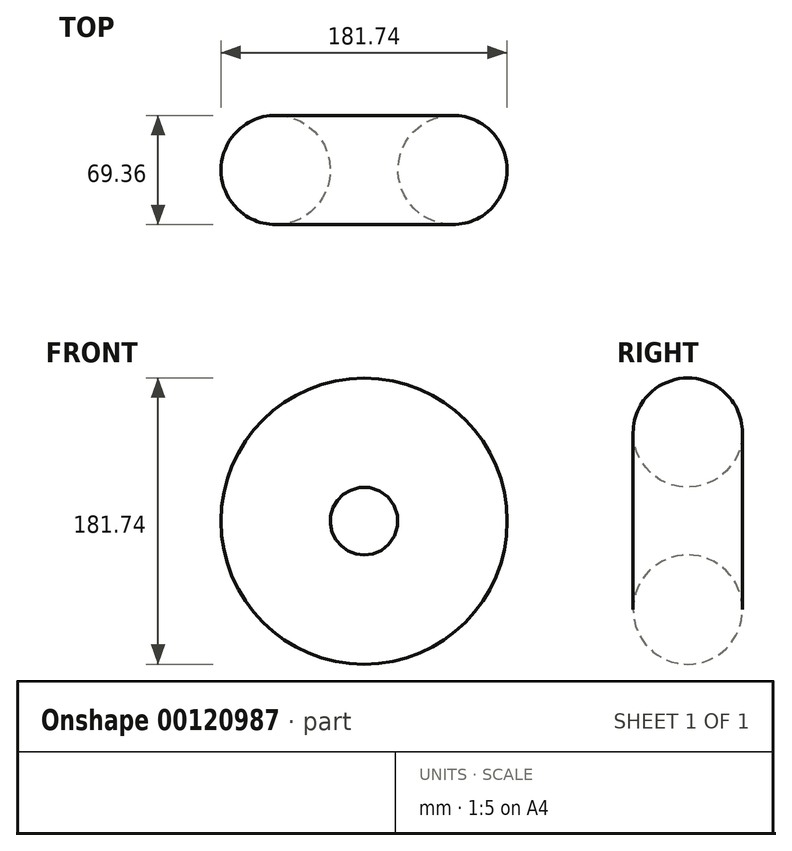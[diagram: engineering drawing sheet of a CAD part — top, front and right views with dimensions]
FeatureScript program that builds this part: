
annotation { "Feature Type Name" : "Feature", "Feature Type Description" : "" }
export const myFeature = defineFeature(function(context is Context, id is Id, definition is map)
    precondition{}
    {
        {
            var Q0;
            Q0=qCreatedBy(makeId("Top.planeOp"),FACE);
            var sketch = newSketch(context, id + "F0", { "sketchPlane" : qUnion([Q0])});
            skCircle(sketch, "E0", {"center": v(56.2, 0) * mm, "radius": 34.68 * mm});
            skLineSegment(sketch, "E1", {"start": v(0, -45.21) * mm, "end": v(0, 44.35) * mm});
            skSolve(sketch);
        }
        {
            var Q0;
            Q0=makeQuery(id+"F0.imprint","IMPRINT",FACE,{"disambiguationData":[TD([[makeQuery(id+"F0.imprint","IMPRINT",EDGE,{"derivedFrom":sQuery(id+"F0.wireOp",EDGE,"E0")}),1.0]])]});
            var Q1;
            Q1=sQuery(id+"F0.wireOp",EDGE,"E1");
            revolve(context, id + "F1", {"entities" : qUnion([Q0]), "axis" : qUnion([Q1]), "revolveType" : RevolveType.FULL});
        }
    });
